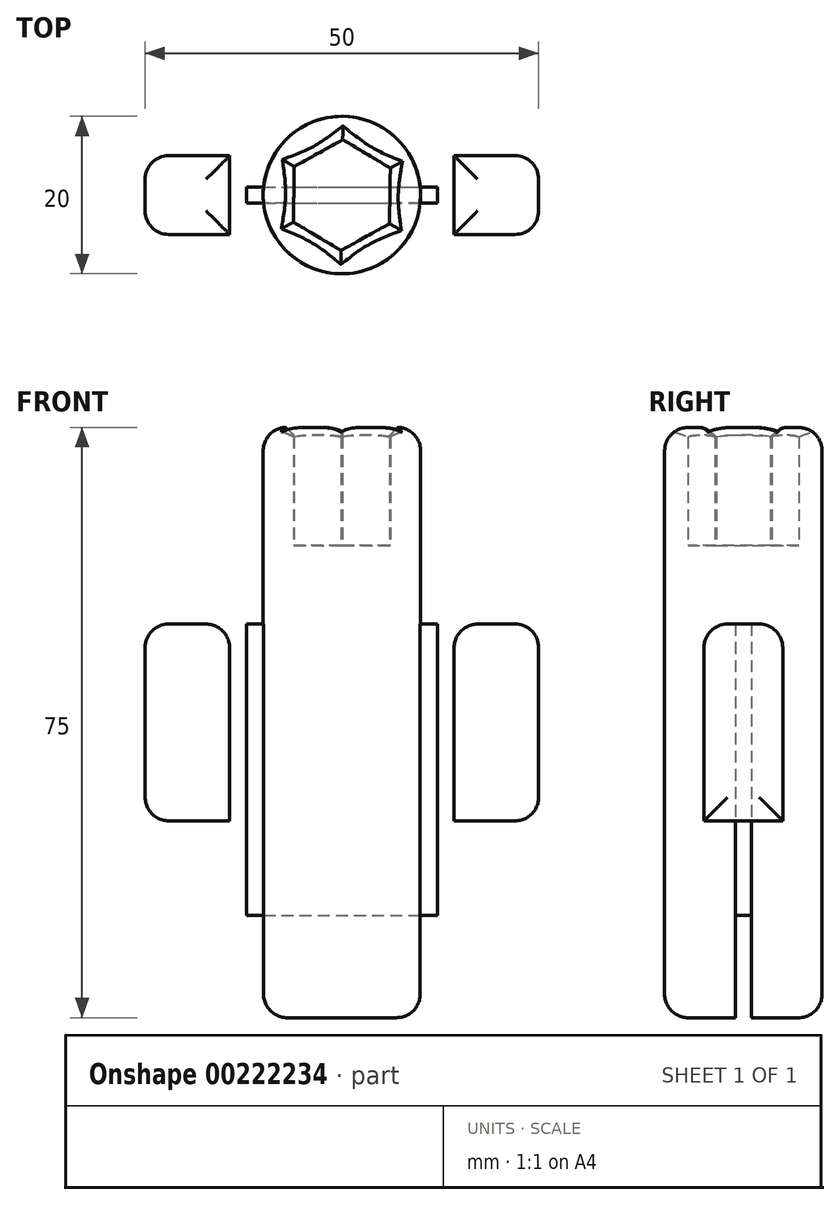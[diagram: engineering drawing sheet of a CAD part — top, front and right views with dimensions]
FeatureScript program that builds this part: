
annotation { "Feature Type Name" : "Feature", "Feature Type Description" : "" }
export const myFeature = defineFeature(function(context is Context, id is Id, definition is map)
    precondition{}
    {
        {
            var Q0;
            Q0=qCreatedBy(makeId("Top.planeOp"),FACE);
            var sketch = newSketch(context, id + "F0", { "sketchPlane" : qUnion([Q0])});
            skPoint(sketch, "E0", {"position": v(5.9, 0) * mm});
            skPoint(sketch, "E1", {"position": v(-6, 0) * mm});
            skPoint(sketch, "E2.0.midPoint", {"position": v(-3.03, 5.1) * mm});
            skCircle(sketch, "E3", {"center": v(0, 0) * mm, "radius": 10 * mm});
            skLineSegment(sketch, "E4.bottom", {"start": v(-12.13, 1) * mm, "end": v(12.12, 1) * mm});
            skLineSegment(sketch, "E4.top", {"start": v(-12.12, -1) * mm, "end": v(12.12, -1) * mm});
            skLineSegment(sketch, "E4.left", {"start": v(-12.12, 1) * mm, "end": v(-12.12, -1) * mm});
            skLineSegment(sketch, "E4.right", {"start": v(12.12, 1) * mm, "end": v(12.12, -1) * mm});
            skLineSegment(sketch, "E5.bottom", {"start": v(-25, 5) * mm, "end": v(25, 5) * mm});
            skLineSegment(sketch, "E5.top", {"start": v(-25, -5) * mm, "end": v(25, -5) * mm});
            skLineSegment(sketch, "E5.left", {"start": v(-25, 5) * mm, "end": v(-25, -5) * mm});
            skLineSegment(sketch, "E5.right", {"start": v(25, 5) * mm, "end": v(25, -5) * mm});
            skPoint(sketch, "E6", {"position": v(0, 7.02) * mm});
            skCircle(sketch, "E7.cCircle", {"center": v(0, 0) * mm, "radius": 6.1 * mm, "construction": true});
            skLineSegment(sketch, "E7.0", {"start": v(-6.05, 3.62) * mm, "end": v(0.1, 7.05) * mm});
            skLineSegment(sketch, "E7.1", {"start": v(0.1, 7.05) * mm, "end": v(6.16, 3.43) * mm});
            skLineSegment(sketch, "E7.2", {"start": v(6.16, 3.43) * mm, "end": v(6.05, -3.62) * mm});
            skLineSegment(sketch, "E7.3", {"start": v(6.05, -3.62) * mm, "end": v(-0.1, -7.05) * mm});
            skLineSegment(sketch, "E7.4", {"start": v(-0.1, -7.05) * mm, "end": v(-6.16, -3.43) * mm});
            skLineSegment(sketch, "E7.5", {"start": v(-6.16, -3.43) * mm, "end": v(-6.05, 3.62) * mm});
            skPoint(sketch, "E7.0.midPoint", {"position": v(-2.97, 5.33) * mm});
            skPoint(sketch, "E8", {"position": v(-10, 0) * mm});
            skPoint(sketch, "E9", {"position": v(-12.12, 0) * mm});
            skPoint(sketch, "E10", {"position": v(-14.25, 0) * mm});
            skPoint(sketch, "E11", {"position": v(14.25, 0) * mm});
            skPoint(sketch, "E12", {"position": v(12.12, 0) * mm});
            skPoint(sketch, "E13", {"position": v(-14.25, 5) * mm});
            skPoint(sketch, "E14", {"position": v(-14.25, -5) * mm});
            skPoint(sketch, "E15", {"position": v(14.25, 5) * mm});
            skPoint(sketch, "E16", {"position": v(14.25, -5) * mm});
            skLineSegment(sketch, "E17", {"start": v(-14.25, 5) * mm, "end": v(-14.25, -5) * mm});
            skLineSegment(sketch, "E18", {"start": v(14.25, 5) * mm, "end": v(14.25, -5) * mm});
            skSolve(sketch);
        }
        {
            var Q0;
            {var subQ0=sQuery(id+"F0.wireOp",EDGE,"E5.top");var subQ1=sQuery(id+"F0.wireOp",EDGE,"E3");var subQ5=makeQuery(id+"F0.imprint","INTERSECT",VERTEX,{"disambiguationData":[OD(0.0)],"derivedFrom":[subQ1,subQ0]});Q0=makeQuery(id+"F0.imprint","IMPRINT",FACE,{"disambiguationData":[TD([[makeQuery(id+"F0.imprint","IMPRINT",EDGE,{"disambiguationData":[TD([[subQ5,-1.0]])],"derivedFrom":subQ1}),1.0]])]});}
            var Q1;
            {var subQ5=sQuery(id+"F0.wireOp",EDGE,"E3");var subQ7=sQuery(id+"F0.wireOp",EDGE,"E5.top");var subQ8=makeQuery(id+"F0.imprint","INTERSECT",VERTEX,{"disambiguationData":[OD(1.0)],"derivedFrom":[subQ5,subQ7]});Q1=makeQuery(id+"F0.imprint","IMPRINT",FACE,{"disambiguationData":[TD([[makeQuery(id+"F0.imprint","IMPRINT",EDGE,{"disambiguationData":[TD([[subQ8,-1.0]])],"derivedFrom":subQ5}),1.0]])]});}
            var Q2;
            {var subQ0=sQuery(id+"F0.wireOp",EDGE,"E4.bottom");var subQ1=sQuery(id+"F0.wireOp",EDGE,"E3");var subQ2=makeQuery(id+"F0.imprint","INTERSECT",VERTEX,{"disambiguationData":[OD(0.0)],"derivedFrom":[subQ1,subQ0]});Q2=makeQuery(id+"F0.imprint","IMPRINT",FACE,{"disambiguationData":[TD([[makeQuery(id+"F0.imprint","IMPRINT",EDGE,{"disambiguationData":[TD([[subQ2,1.0]])],"derivedFrom":subQ1}),1.0]])]});}
            var Q3;
            {var subQ0=sQuery(id+"F0.wireOp",EDGE,"E5.bottom");var subQ1=sQuery(id+"F0.wireOp",EDGE,"E3");var subQ2=makeQuery(id+"F0.imprint","INTERSECT",VERTEX,{"disambiguationData":[OD(0.0)],"derivedFrom":[subQ1,subQ0]});Q3=makeQuery(id+"F0.imprint","IMPRINT",FACE,{"disambiguationData":[TD([[makeQuery(id+"F0.imprint","IMPRINT",EDGE,{"disambiguationData":[TD([[subQ2,1.0]])],"derivedFrom":subQ1}),1.0]])]});}
            var Q4;
            {var subQ3=sQuery(id+"F0.wireOp",EDGE,"E5.bottom");var subQ5=sQuery(id+"F0.wireOp",EDGE,"E3");var subQ6=makeQuery(id+"F0.imprint","INTERSECT",VERTEX,{"disambiguationData":[OD(0.0)],"derivedFrom":[subQ5,subQ3]});Q4=makeQuery(id+"F0.imprint","IMPRINT",FACE,{"disambiguationData":[TD([[makeQuery(id+"F0.imprint","IMPRINT",EDGE,{"disambiguationData":[TD([[subQ6,-1.0]])],"derivedFrom":subQ5}),1.0]])]});}
            var Q5;
            {var subQ0=sQuery(id+"F0.wireOp",EDGE,"E5.bottom");var subQ1=sQuery(id+"F0.wireOp",EDGE,"E3");var subQ2=makeQuery(id+"F0.imprint","INTERSECT",VERTEX,{"disambiguationData":[OD(1.0)],"derivedFrom":[subQ1,subQ0]});Q5=makeQuery(id+"F0.imprint","IMPRINT",FACE,{"disambiguationData":[TD([[makeQuery(id+"F0.imprint","IMPRINT",EDGE,{"disambiguationData":[TD([[subQ2,-1.0]])],"derivedFrom":subQ1}),1.0]])]});}
            var Q6;
            {var subQ3=sQuery(id+"F0.wireOp",EDGE,"E5.top");var subQ5=sQuery(id+"F0.wireOp",EDGE,"E3");var subQ6=makeQuery(id+"F0.imprint","INTERSECT",VERTEX,{"disambiguationData":[OD(0.0)],"derivedFrom":[subQ5,subQ3]});Q6=makeQuery(id+"F0.imprint","IMPRINT",FACE,{"disambiguationData":[TD([[makeQuery(id+"F0.imprint","IMPRINT",EDGE,{"disambiguationData":[TD([[subQ6,1.0]])],"derivedFrom":subQ5}),1.0]])]});}
            var Q7;
            {var subQ0=sQuery(id+"F0.wireOp",EDGE,"E4.bottom");var subQ1=sQuery(id+"F0.wireOp",EDGE,"E3");var subQ2=makeQuery(id+"F0.imprint","INTERSECT",VERTEX,{"disambiguationData":[OD(1.0)],"derivedFrom":[subQ1,subQ0]});Q7=makeQuery(id+"F0.imprint","IMPRINT",FACE,{"disambiguationData":[TD([[makeQuery(id+"F0.imprint","IMPRINT",EDGE,{"disambiguationData":[TD([[subQ2,-1.0]])],"derivedFrom":subQ1}),1.0]])]});}
            extrude(context, id + "F1", {"entities" : qUnion([Q0, Q1, Q2, Q3, Q4, Q5, Q6, Q7]), "depth" : 50 * mm});
        }
        {
            var Q0;
            {var subQ0=sQuery(id+"F0.wireOp",EDGE,"E4.left");Q0=makeQuery(id+"F0.imprint","IMPRINT",FACE,{"disambiguationData":[TD([[makeQuery(id+"F0.imprint","IMPRINT",EDGE,{"derivedFrom":subQ0}),-1.0]])]});}
            var Q1;
            {var subQ5=sQuery(id+"F0.wireOp",EDGE,"E4.left");Q1=makeQuery(id+"F0.imprint","IMPRINT",FACE,{"disambiguationData":[TD([[makeQuery(id+"F0.imprint","IMPRINT",EDGE,{"derivedFrom":subQ5}),1.0]])]});}
            var Q2;
            {var subQ0=sQuery(id+"F0.wireOp",EDGE,"E4.right");Q2=makeQuery(id+"F0.imprint","IMPRINT",FACE,{"disambiguationData":[TD([[makeQuery(id+"F0.imprint","IMPRINT",EDGE,{"derivedFrom":subQ0}),1.0]])]});}
            var Q3;
            {var subQ5=sQuery(id+"F0.wireOp",EDGE,"E4.right");Q3=makeQuery(id+"F0.imprint","IMPRINT",FACE,{"disambiguationData":[TD([[makeQuery(id+"F0.imprint","IMPRINT",EDGE,{"derivedFrom":subQ5}),-1.0]])]});}
            var Q4;
            {var subQ0=sQuery(id+"F0.wireOp",EDGE,"E5.left");Q4=makeQuery(id+"F0.imprint","IMPRINT",FACE,{"disambiguationData":[TD([[makeQuery(id+"F0.imprint","IMPRINT",EDGE,{"derivedFrom":subQ0}),1.0]])]});}
            var Q5;
            {var subQ0=sQuery(id+"F0.wireOp",EDGE,"E5.right");Q5=makeQuery(id+"F0.imprint","IMPRINT",FACE,{"disambiguationData":[TD([[makeQuery(id+"F0.imprint","IMPRINT",EDGE,{"derivedFrom":subQ0}),-1.0]])]});}
            extrude(context, id + "F2", {"entities" : qUnion([Q0, Q1, Q2, Q3, Q4, Q5]), "operationType" : NewBodyOperationType.ADD, "depth" : 25 * mm});
        }
        {
            var Q0;
            {var subQ5=sQuery(id+"F0.wireOp",EDGE,"E4.top");var subQ9=sQuery(id+"F0.wireOp",EDGE,"E7.5");var subQ10=makeQuery(id+"F0.imprint","INTERSECT",VERTEX,{"derivedFrom":[subQ5,subQ9]});Q0=makeQuery(id+"F0.imprint","IMPRINT",FACE,{"disambiguationData":[TD([[makeQuery(id+"F0.imprint","IMPRINT",EDGE,{"disambiguationData":[TD([[subQ10,-1.0]])],"derivedFrom":subQ5}),-1.0]])]});}
            var Q1;
            {var subQ0=sQuery(id+"F0.wireOp",EDGE,"E7.4");var subQ1=sQuery(id+"F0.wireOp",EDGE,"E5.top");var subQ2=makeQuery(id+"F0.imprint","INTERSECT",VERTEX,{"derivedFrom":[subQ1,subQ0]});Q1=makeQuery(id+"F0.imprint","IMPRINT",FACE,{"disambiguationData":[TD([[makeQuery(id+"F0.imprint","IMPRINT",EDGE,{"disambiguationData":[TD([[subQ2,-1.0]])],"derivedFrom":subQ1}),-1.0]])]});}
            var Q2;
            {var subQ0=sQuery(id+"F0.wireOp",EDGE,"E7.5");var subQ1=sQuery(id+"F0.wireOp",EDGE,"E4.bottom");var subQ2=makeQuery(id+"F0.imprint","INTERSECT",VERTEX,{"derivedFrom":[subQ1,subQ0]});Q2=makeQuery(id+"F0.imprint","IMPRINT",FACE,{"disambiguationData":[TD([[makeQuery(id+"F0.imprint","IMPRINT",EDGE,{"disambiguationData":[TD([[subQ2,-1.0]])],"derivedFrom":subQ1}),-1.0]])]});}
            var Q3;
            {var subQ0=sQuery(id+"F0.wireOp",EDGE,"E7.5");var subQ5=sQuery(id+"F0.wireOp",EDGE,"E4.bottom");var subQ6=makeQuery(id+"F0.imprint","INTERSECT",VERTEX,{"derivedFrom":[subQ5,subQ0]});Q3=makeQuery(id+"F0.imprint","IMPRINT",FACE,{"disambiguationData":[TD([[makeQuery(id+"F0.imprint","IMPRINT",EDGE,{"disambiguationData":[TD([[subQ6,-1.0]])],"derivedFrom":subQ5}),1.0]])]});}
            var Q4;
            {var subQ0=sQuery(id+"F0.wireOp",EDGE,"E7.0");var subQ1=sQuery(id+"F0.wireOp",EDGE,"E5.bottom");var subQ2=makeQuery(id+"F0.imprint","INTERSECT",VERTEX,{"derivedFrom":[subQ1,subQ0]});Q4=makeQuery(id+"F0.imprint","IMPRINT",FACE,{"disambiguationData":[TD([[makeQuery(id+"F0.imprint","IMPRINT",EDGE,{"disambiguationData":[TD([[subQ2,-1.0]])],"derivedFrom":subQ1}),1.0]])]});}
            extrude(context, id + "F3", {"entities" : qUnion([Q0, Q1, Q2, Q3, Q4]), "operationType" : NewBodyOperationType.ADD, "depth" : 35 * mm});
        }
        {
            var Q0;
            {var subQ0=sQuery(id+"F0.wireOp",EDGE,"E4.right");Q0=makeQuery(id+"F0.imprint","IMPRINT",FACE,{"disambiguationData":[TD([[makeQuery(id+"F0.imprint","IMPRINT",EDGE,{"derivedFrom":subQ0}),1.0]])]});}
            var Q1;
            {var subQ3=sQuery(id+"F0.wireOp",EDGE,"E5.bottom");var subQ5=sQuery(id+"F0.wireOp",EDGE,"E3");var subQ6=makeQuery(id+"F0.imprint","INTERSECT",VERTEX,{"disambiguationData":[OD(0.0)],"derivedFrom":[subQ5,subQ3]});Q1=makeQuery(id+"F0.imprint","IMPRINT",FACE,{"disambiguationData":[TD([[makeQuery(id+"F0.imprint","IMPRINT",EDGE,{"disambiguationData":[TD([[subQ6,1.0]])],"derivedFrom":subQ5}),1.0]])]});}
            var Q2;
            {var subQ0=sQuery(id+"F0.wireOp",EDGE,"E5.bottom");var subQ1=sQuery(id+"F0.wireOp",EDGE,"E3");var subQ2=makeQuery(id+"F0.imprint","INTERSECT",VERTEX,{"disambiguationData":[OD(0.0)],"derivedFrom":[subQ1,subQ0]});Q2=makeQuery(id+"F0.imprint","IMPRINT",FACE,{"disambiguationData":[TD([[makeQuery(id+"F0.imprint","IMPRINT",EDGE,{"disambiguationData":[TD([[subQ2,-1.0]])],"derivedFrom":subQ1}),1.0]])]});}
            var Q3;
            {var subQ3=sQuery(id+"F0.wireOp",EDGE,"E5.bottom");var subQ6=sQuery(id+"F0.wireOp",EDGE,"E3");var subQ9=makeQuery(id+"F0.imprint","INTERSECT",VERTEX,{"disambiguationData":[OD(1.0)],"derivedFrom":[subQ6,subQ3]});Q3=makeQuery(id+"F0.imprint","IMPRINT",FACE,{"disambiguationData":[TD([[makeQuery(id+"F0.imprint","IMPRINT",EDGE,{"disambiguationData":[TD([[subQ9,-1.0]])],"derivedFrom":subQ6}),1.0]])]});}
            var Q4;
            {var subQ5=sQuery(id+"F0.wireOp",EDGE,"E7.5");var subQ9=sQuery(id+"F0.wireOp",EDGE,"E4.bottom");var subQ10=makeQuery(id+"F0.imprint","INTERSECT",VERTEX,{"derivedFrom":[subQ9,subQ5]});Q4=makeQuery(id+"F0.imprint","IMPRINT",FACE,{"disambiguationData":[TD([[makeQuery(id+"F0.imprint","IMPRINT",EDGE,{"disambiguationData":[TD([[subQ10,-1.0]])],"derivedFrom":subQ9}),1.0]])]});}
            var Q5;
            {var subQ0=sQuery(id+"F0.wireOp",EDGE,"E7.0");var subQ1=sQuery(id+"F0.wireOp",EDGE,"E5.bottom");var subQ2=makeQuery(id+"F0.imprint","INTERSECT",VERTEX,{"derivedFrom":[subQ1,subQ0]});Q5=makeQuery(id+"F0.imprint","IMPRINT",FACE,{"disambiguationData":[TD([[makeQuery(id+"F0.imprint","IMPRINT",EDGE,{"disambiguationData":[TD([[subQ2,-1.0]])],"derivedFrom":subQ1}),1.0]])]});}
            var Q6;
            {var subQ0=sQuery(id+"F0.wireOp",EDGE,"E4.left");Q6=makeQuery(id+"F0.imprint","IMPRINT",FACE,{"disambiguationData":[TD([[makeQuery(id+"F0.imprint","IMPRINT",EDGE,{"derivedFrom":subQ0}),-1.0]])]});}
            var Q7;
            {var subQ3=sQuery(id+"F0.wireOp",EDGE,"E5.top");var subQ5=sQuery(id+"F0.wireOp",EDGE,"E3");var subQ6=makeQuery(id+"F0.imprint","INTERSECT",VERTEX,{"disambiguationData":[OD(0.0)],"derivedFrom":[subQ5,subQ3]});Q7=makeQuery(id+"F0.imprint","IMPRINT",FACE,{"disambiguationData":[TD([[makeQuery(id+"F0.imprint","IMPRINT",EDGE,{"disambiguationData":[TD([[subQ6,1.0]])],"derivedFrom":subQ5}),1.0]])]});}
            var Q8;
            {var subQ0=sQuery(id+"F0.wireOp",EDGE,"E5.top");var subQ1=sQuery(id+"F0.wireOp",EDGE,"E3");var subQ7=makeQuery(id+"F0.imprint","INTERSECT",VERTEX,{"disambiguationData":[OD(0.0)],"derivedFrom":[subQ1,subQ0]});Q8=makeQuery(id+"F0.imprint","IMPRINT",FACE,{"disambiguationData":[TD([[makeQuery(id+"F0.imprint","IMPRINT",EDGE,{"disambiguationData":[TD([[subQ7,-1.0]])],"derivedFrom":subQ1}),1.0]])]});}
            var Q9;
            {var subQ5=sQuery(id+"F0.wireOp",EDGE,"E5.top");var subQ6=sQuery(id+"F0.wireOp",EDGE,"E3");var subQ7=makeQuery(id+"F0.imprint","INTERSECT",VERTEX,{"disambiguationData":[OD(1.0)],"derivedFrom":[subQ6,subQ5]});Q9=makeQuery(id+"F0.imprint","IMPRINT",FACE,{"disambiguationData":[TD([[makeQuery(id+"F0.imprint","IMPRINT",EDGE,{"disambiguationData":[TD([[subQ7,-1.0]])],"derivedFrom":subQ6}),1.0]])]});}
            var Q10;
            {var subQ5=sQuery(id+"F0.wireOp",EDGE,"E4.top");var subQ9=sQuery(id+"F0.wireOp",EDGE,"E7.5");var subQ10=makeQuery(id+"F0.imprint","INTERSECT",VERTEX,{"derivedFrom":[subQ5,subQ9]});Q10=makeQuery(id+"F0.imprint","IMPRINT",FACE,{"disambiguationData":[TD([[makeQuery(id+"F0.imprint","IMPRINT",EDGE,{"disambiguationData":[TD([[subQ10,-1.0]])],"derivedFrom":subQ5}),-1.0]])]});}
            var Q11;
            {var subQ0=sQuery(id+"F0.wireOp",EDGE,"E7.4");var subQ1=sQuery(id+"F0.wireOp",EDGE,"E5.top");var subQ2=makeQuery(id+"F0.imprint","INTERSECT",VERTEX,{"derivedFrom":[subQ1,subQ0]});Q11=makeQuery(id+"F0.imprint","IMPRINT",FACE,{"disambiguationData":[TD([[makeQuery(id+"F0.imprint","IMPRINT",EDGE,{"disambiguationData":[TD([[subQ2,-1.0]])],"derivedFrom":subQ1}),-1.0]])]});}
            extrude(context, id + "F4", {"entities" : qUnion([Q0, Q1, Q2, Q3, Q4, Q5, Q6, Q7, Q8, Q9, Q10, Q11]), "operationType" : NewBodyOperationType.ADD, "oppositeDirection" : true, "depth" : 25 * mm});
        }
        {
            var Q0;
            {var subQ5=sQuery(id+"F0.wireOp",EDGE,"E4.right");Q0=makeQuery(id+"F0.imprint","IMPRINT",FACE,{"disambiguationData":[TD([[makeQuery(id+"F0.imprint","IMPRINT",EDGE,{"derivedFrom":subQ5}),-1.0]])]});}
            var Q1;
            {var subQ0=sQuery(id+"F0.wireOp",EDGE,"E4.bottom");var subQ1=sQuery(id+"F0.wireOp",EDGE,"E3");var subQ2=makeQuery(id+"F0.imprint","INTERSECT",VERTEX,{"disambiguationData":[OD(0.0)],"derivedFrom":[subQ1,subQ0]});Q1=makeQuery(id+"F0.imprint","IMPRINT",FACE,{"disambiguationData":[TD([[makeQuery(id+"F0.imprint","IMPRINT",EDGE,{"disambiguationData":[TD([[subQ2,1.0]])],"derivedFrom":subQ1}),1.0]])]});}
            var Q2;
            {var subQ0=sQuery(id+"F0.wireOp",EDGE,"E7.5");var subQ1=sQuery(id+"F0.wireOp",EDGE,"E4.bottom");var subQ2=makeQuery(id+"F0.imprint","INTERSECT",VERTEX,{"derivedFrom":[subQ1,subQ0]});Q2=makeQuery(id+"F0.imprint","IMPRINT",FACE,{"disambiguationData":[TD([[makeQuery(id+"F0.imprint","IMPRINT",EDGE,{"disambiguationData":[TD([[subQ2,-1.0]])],"derivedFrom":subQ1}),-1.0]])]});}
            var Q3;
            {var subQ0=sQuery(id+"F0.wireOp",EDGE,"E4.bottom");var subQ1=sQuery(id+"F0.wireOp",EDGE,"E3");var subQ2=makeQuery(id+"F0.imprint","INTERSECT",VERTEX,{"disambiguationData":[OD(1.0)],"derivedFrom":[subQ1,subQ0]});Q3=makeQuery(id+"F0.imprint","IMPRINT",FACE,{"disambiguationData":[TD([[makeQuery(id+"F0.imprint","IMPRINT",EDGE,{"disambiguationData":[TD([[subQ2,-1.0]])],"derivedFrom":subQ1}),1.0]])]});}
            var Q4;
            {var subQ5=sQuery(id+"F0.wireOp",EDGE,"E4.left");Q4=makeQuery(id+"F0.imprint","IMPRINT",FACE,{"disambiguationData":[TD([[makeQuery(id+"F0.imprint","IMPRINT",EDGE,{"derivedFrom":subQ5}),1.0]])]});}
            extrude(context, id + "F5", {"entities" : qUnion([Q0, Q1, Q2, Q3, Q4]), "operationType" : NewBodyOperationType.ADD, "oppositeDirection" : true, "depth" : 12 * mm});
        }
        {
            var Q0;
            Q0=makeQuery(id+"F2.opExtrude","SWEPT_FACE",FACE,{"disambiguationData":[OSD([sQuery(id+"F0.wireOp",EDGE,"E5.right")])]});
            var Q1;
            Q1=makeQuery(id+"F4.opExtrude","SWEPT_FACE",FACE,{"disambiguationData":[OSD([sQuery(id+"F0.wireOp",EDGE,"E18")])]});
            var Q2;
            Q2=makeQuery(id+"F4.opExtrude","SWEPT_FACE",FACE,{"disambiguationData":[OSD([sQuery(id+"F0.wireOp",EDGE,"E17")])]});
            var Q3;
            Q3=makeQuery(id+"F2.opExtrude","SWEPT_FACE",FACE,{"disambiguationData":[OSD([sQuery(id+"F0.wireOp",EDGE,"E5.left")])]});
            var Q4;
            Q4=makeQuery(id+"F2.opExtrude","CAP_FACE",FACE,{"disambiguationData":[OSD([sQuery(id+"F0.wireOp",EDGE,"E3"),sQuery(id+"F0.wireOp",EDGE,"E5.bottom"),sQuery(id+"F0.wireOp",EDGE,"E5.top"),sQuery(id+"F0.wireOp",EDGE,"E5.left")])],"isStart":false});
            var Q5;
            Q5=makeQuery(id+"F2.opExtrude","CAP_FACE",FACE,{"disambiguationData":[OSD([sQuery(id+"F0.wireOp",EDGE,"E3"),sQuery(id+"F0.wireOp",EDGE,"E5.bottom"),sQuery(id+"F0.wireOp",EDGE,"E5.top"),sQuery(id+"F0.wireOp",EDGE,"E5.right")])],"isStart":false});
            var Q6;
            Q6=makeQuery(id+"F1.opExtrude","CAP_EDGE",EDGE,{"disambiguationData":[OSD([sQuery(id+"F0.wireOp",EDGE,"E3")])],"isStart":false});
            var Q7;
            {var subQ1=sQuery(id+"F0.wireOp",EDGE,"E5.bottom");var subQ3=sQuery(id+"F0.wireOp",EDGE,"E3");var subQ5=sQuery(id+"F0.wireOp",EDGE,"E5.left");var subQ6=sQuery(id+"F0.wireOp",EDGE,"E5.top");var subQ9=sQuery(id+"F0.wireOp",EDGE,"E7.5");var subQ10=sQuery(id+"F0.wireOp",EDGE,"E7.4");var subQ11=sQuery(id+"F0.wireOp",EDGE,"E7.3");var subQ12=sQuery(id+"F0.wireOp",EDGE,"E7.2");var subQ13=sQuery(id+"F0.wireOp",EDGE,"E7.1");var subQ14=sQuery(id+"F0.wireOp",EDGE,"E7.0");Q7=makeQuery(id+"F4.boolean.opBoolean","SPLIT",FACE,{"disambiguationData":[TD([makeQuery(id+"F2.opExtrude","SWEPT_FACE",FACE,{"disambiguationData":[OSD([subQ5])]})])],"derivedFrom":makeQuery(id+"F3.boolean.opBoolean","MERGE",FACE,{"derivedFrom":[makeQuery(id+"F2.boolean.opBoolean","MERGE",FACE,{"derivedFrom":[makeQuery(id+"F1.opExtrude","CAP_FACE",FACE,{"disambiguationData":[OSD([subQ3,subQ14,subQ13,subQ12,subQ11,subQ10,subQ9])],"isStart":true}),makeQuery(id+"F2.opExtrude","CAP_FACE",FACE,{"disambiguationData":[OSD([subQ3,subQ1,subQ6,sQuery(id+"F0.wireOp",EDGE,"E5.right")])],"isStart":true}),makeQuery(id+"F2.opExtrude","CAP_FACE",FACE,{"disambiguationData":[OSD([subQ3,subQ1,subQ6,subQ5])],"isStart":true})]}),makeQuery(id+"F3.opExtrude","CAP_FACE",FACE,{"disambiguationData":[OSD([subQ14,subQ13,subQ12,subQ11,subQ10,subQ9])],"isStart":true})]})});}
            var Q8;
            {var subQ1=sQuery(id+"F0.wireOp",EDGE,"E5.bottom");var subQ3=sQuery(id+"F0.wireOp",EDGE,"E3");var subQ5=sQuery(id+"F0.wireOp",EDGE,"E5.right");var subQ6=sQuery(id+"F0.wireOp",EDGE,"E5.top");var subQ9=sQuery(id+"F0.wireOp",EDGE,"E7.5");var subQ10=sQuery(id+"F0.wireOp",EDGE,"E7.4");var subQ11=sQuery(id+"F0.wireOp",EDGE,"E7.3");var subQ12=sQuery(id+"F0.wireOp",EDGE,"E7.2");var subQ13=sQuery(id+"F0.wireOp",EDGE,"E7.1");var subQ14=sQuery(id+"F0.wireOp",EDGE,"E7.0");Q8=makeQuery(id+"F4.boolean.opBoolean","SPLIT",FACE,{"disambiguationData":[TD([makeQuery(id+"F2.opExtrude","SWEPT_FACE",FACE,{"disambiguationData":[OSD([subQ5])]})])],"derivedFrom":makeQuery(id+"F3.boolean.opBoolean","MERGE",FACE,{"derivedFrom":[makeQuery(id+"F2.boolean.opBoolean","MERGE",FACE,{"derivedFrom":[makeQuery(id+"F1.opExtrude","CAP_FACE",FACE,{"disambiguationData":[OSD([subQ3,subQ14,subQ13,subQ12,subQ11,subQ10,subQ9])],"isStart":true}),makeQuery(id+"F2.opExtrude","CAP_FACE",FACE,{"disambiguationData":[OSD([subQ3,subQ1,subQ6,subQ5])],"isStart":true}),makeQuery(id+"F2.opExtrude","CAP_FACE",FACE,{"disambiguationData":[OSD([subQ3,subQ1,subQ6,sQuery(id+"F0.wireOp",EDGE,"E5.left")])],"isStart":true})]}),makeQuery(id+"F3.opExtrude","CAP_FACE",FACE,{"disambiguationData":[OSD([subQ14,subQ13,subQ12,subQ11,subQ10,subQ9])],"isStart":true})]})});}
            var Q9;
            {var subQ0=sQuery(id+"F0.wireOp",EDGE,"E5.bottom");var subQ1=sQuery(id+"F0.wireOp",EDGE,"E3");Q9=makeQuery(id+"F4.opExtrude","CAP_EDGE",EDGE,{"disambiguationData":[OSD([subQ1]),TDD([makeQuery(id+"F0.imprint","IMPRINT",EDGE,{"disambiguationData":[TD([[makeQuery(id+"F0.imprint","INTERSECT",VERTEX,{"disambiguationData":[OD(0.0)],"derivedFrom":[subQ1,subQ0]}),-1.0]])],"derivedFrom":subQ1})])],"isStart":false});}
            var Q10;
            {var subQ0=sQuery(id+"F0.wireOp",EDGE,"E5.bottom");Q10=makeQuery(id+"F4.opExtrude","CAP_EDGE",EDGE,{"disambiguationData":[OSD([subQ0]),TDD([makeQuery(id+"F0.imprint","IMPRINT",EDGE,{"disambiguationData":[TD([[makeQuery(id+"F0.imprint","INTERSECT",VERTEX,{"derivedFrom":[subQ0,sQuery(id+"F0.wireOp",EDGE,"E18")]}),1.0]])],"derivedFrom":subQ0})])],"isStart":false});}
            var Q11;
            {var subQ0=sQuery(id+"F0.wireOp",EDGE,"E5.top");Q11=makeQuery(id+"F4.opExtrude","CAP_EDGE",EDGE,{"disambiguationData":[OSD([subQ0]),TDD([makeQuery(id+"F0.imprint","IMPRINT",EDGE,{"disambiguationData":[TD([[makeQuery(id+"F0.imprint","INTERSECT",VERTEX,{"derivedFrom":[subQ0,sQuery(id+"F0.wireOp",EDGE,"E18")]}),1.0]])],"derivedFrom":subQ0})])],"isStart":false});}
            var Q12;
            {var subQ0=sQuery(id+"F0.wireOp",EDGE,"E5.top");var subQ1=sQuery(id+"F0.wireOp",EDGE,"E3");Q12=makeQuery(id+"F4.opExtrude","CAP_EDGE",EDGE,{"disambiguationData":[OSD([subQ1]),TDD([makeQuery(id+"F0.imprint","IMPRINT",EDGE,{"disambiguationData":[TD([[makeQuery(id+"F0.imprint","INTERSECT",VERTEX,{"disambiguationData":[OD(0.0)],"derivedFrom":[subQ1,subQ0]}),-1.0]])],"derivedFrom":subQ1})])],"isStart":false});}
            var Q13;
            {var subQ0=sQuery(id+"F0.wireOp",EDGE,"E5.top");Q13=makeQuery(id+"F4.opExtrude","CAP_EDGE",EDGE,{"disambiguationData":[OSD([subQ0]),TDD([makeQuery(id+"F0.imprint","IMPRINT",EDGE,{"disambiguationData":[TD([[makeQuery(id+"F0.imprint","INTERSECT",VERTEX,{"derivedFrom":[subQ0,sQuery(id+"F0.wireOp",EDGE,"E17")]}),-1.0]])],"derivedFrom":subQ0})])],"isStart":false});}
            var Q14;
            Q14=makeQuery(id+"F4.opExtrude","CAP_EDGE",EDGE,{"disambiguationData":[OSD([sQuery(id+"F0.wireOp",EDGE,"E17")])],"isStart":false});
            var Q15;
            {var subQ0=sQuery(id+"F0.wireOp",EDGE,"E5.bottom");Q15=makeQuery(id+"F4.opExtrude","CAP_EDGE",EDGE,{"disambiguationData":[OSD([subQ0]),TDD([makeQuery(id+"F0.imprint","IMPRINT",EDGE,{"disambiguationData":[TD([[makeQuery(id+"F0.imprint","INTERSECT",VERTEX,{"derivedFrom":[subQ0,sQuery(id+"F0.wireOp",EDGE,"E17")]}),-1.0]])],"derivedFrom":subQ0})])],"isStart":false});}
            var Q16;
            Q16=makeQuery(id+"F4.opExtrude","CAP_EDGE",EDGE,{"disambiguationData":[OSD([sQuery(id+"F0.wireOp",EDGE,"E18")])],"isStart":false});
            fillet(context, id + "F6", {"entities" : qUnion([Q0, Q1, Q2, Q3, Q4, Q5, Q6, Q7, Q8, Q9, Q10, Q11, Q12, Q13, Q14, Q15, Q16]), "radius" : 3 * mm, "tangentPropagation" : true, "allowEdgeOverflow" : false});
        }
        {
            var Q0;
            Q0=makeQuery(id+"F1.opExtrude","CAP_EDGE",EDGE,{"disambiguationData":[OSD([sQuery(id+"F0.wireOp",EDGE,"E7.3")])],"isStart":false});
            var Q1;
            Q1=makeQuery(id+"F1.opExtrude","CAP_EDGE",EDGE,{"disambiguationData":[OSD([sQuery(id+"F0.wireOp",EDGE,"E7.4")])],"isStart":false});
            var Q2;
            Q2=makeQuery(id+"F1.opExtrude","CAP_EDGE",EDGE,{"disambiguationData":[OSD([sQuery(id+"F0.wireOp",EDGE,"E7.5")])],"isStart":false});
            var Q3;
            Q3=makeQuery(id+"F1.opExtrude","CAP_EDGE",EDGE,{"disambiguationData":[OSD([sQuery(id+"F0.wireOp",EDGE,"E7.0")])],"isStart":false});
            var Q4;
            Q4=makeQuery(id+"F1.opExtrude","CAP_EDGE",EDGE,{"disambiguationData":[OSD([sQuery(id+"F0.wireOp",EDGE,"E7.1")])],"isStart":false});
            var Q5;
            Q5=makeQuery(id+"F1.opExtrude","CAP_EDGE",EDGE,{"disambiguationData":[OSD([sQuery(id+"F0.wireOp",EDGE,"E7.2")])],"isStart":false});
            chamfer(context, id + "F7", {"entities" : qUnion([Q0, Q1, Q2, Q3, Q4, Q5]), "width" : 1 * mm, "tangentPropagation" : true});
        }
    });
